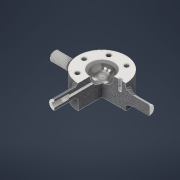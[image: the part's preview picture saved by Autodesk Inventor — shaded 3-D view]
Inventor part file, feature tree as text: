
AUTODESK INVENTOR PART (.ipt)
format: ipt  version: 2022 (Build 260153000, 153)  size: 265,216 bytes
history: native  units: mm
features: sketch x7, extrude x3, chamfer x3, other x2, revolve x2, hole x2, thread x1, mirror x1, pattern_circular x1
ambient origin geometry x8: Origin, YZ Plane, XZ Plane, XY Plane, X Axis, Y Axis, Z Axis, Center Point
bodies: Body1 (feature_tree)
feature tree (22):
  extrude  "Выдавливание4"  Depth=100.0mm
  other  "РабПлоскость10"
  revolve  "Вращение3"
  thread  "Резьба2"
  chamfer  "Фаска2"  Distance=50.0mm
  chamfer  "Фаска3"  Distance=100.0mm
  mirror  "Зеркальное отражение2"
  revolve  "Вращение4"
  hole  "Отверстие4"  [1 undecoded]
  pattern_circular  "Круговой массив2"  [2 undecoded]
  other  "РабПлоскость12"
  extrude  "Выдавливание9"  TaperAngle=15.0deg  [1 undecoded]
  chamfer  "Фаска4"  Angle=90.0deg  [1 undecoded]
  hole  "Отверстие5"  [1 undecoded]
  extrude  "Выдавливание10"  Depth=2.0mm TaperAngle=45.0deg
  sketch  "Эскиз18"
  sketch  "Эскиз19"
  sketch  "Эскиз22"
  sketch  "Эскиз23"
  sketch  "Эскиз28"
  sketch  "Эскиз29"
  sketch  "Эскиз30"
note: 6 required parameter values undecoded (feature->parameter linkage not recoverable at this tier; creation-order binding heuristic only, values carry confidence <= 0.55)
